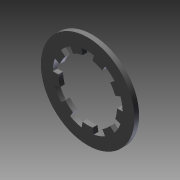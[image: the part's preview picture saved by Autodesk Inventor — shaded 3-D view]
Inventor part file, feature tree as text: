
AUTODESK INVENTOR PART (.ipt)
format: ipt  version: 2015 (Build 190159000, 159)  size: 127,488 bytes
history: native  units: in
note: dims shown in document units (in); Inventor stores cm internally (conversion verified against a paired STEP export)
features: other x7, extrude x1, sketch x1
ambient origin geometry x8: Origin, YZ Plane, XZ Plane, XY Plane, X Axis, Y Axis, Z Axis, Center Point
bodies: Solid1 (feature_tree)
feature tree (9):
  extrude  "Extrusion1"  [1 undecoded]
  other  "lockwasher_XY"
  other  "lockwasher_YZ"
  other  "lockwasher_ZX"
  other  "lockwasher_X"
  other  "lockwasher_Y"
  other  "lockwasher_Z"
  other  "lockwasher_Center"
  sketch  "Sketch_2"  dims[d0=0.02in d1=0.0in]
note: 1 required parameter value undecoded (feature->parameter linkage not recoverable at this tier; creation-order binding heuristic only, values carry confidence <= 0.55)
